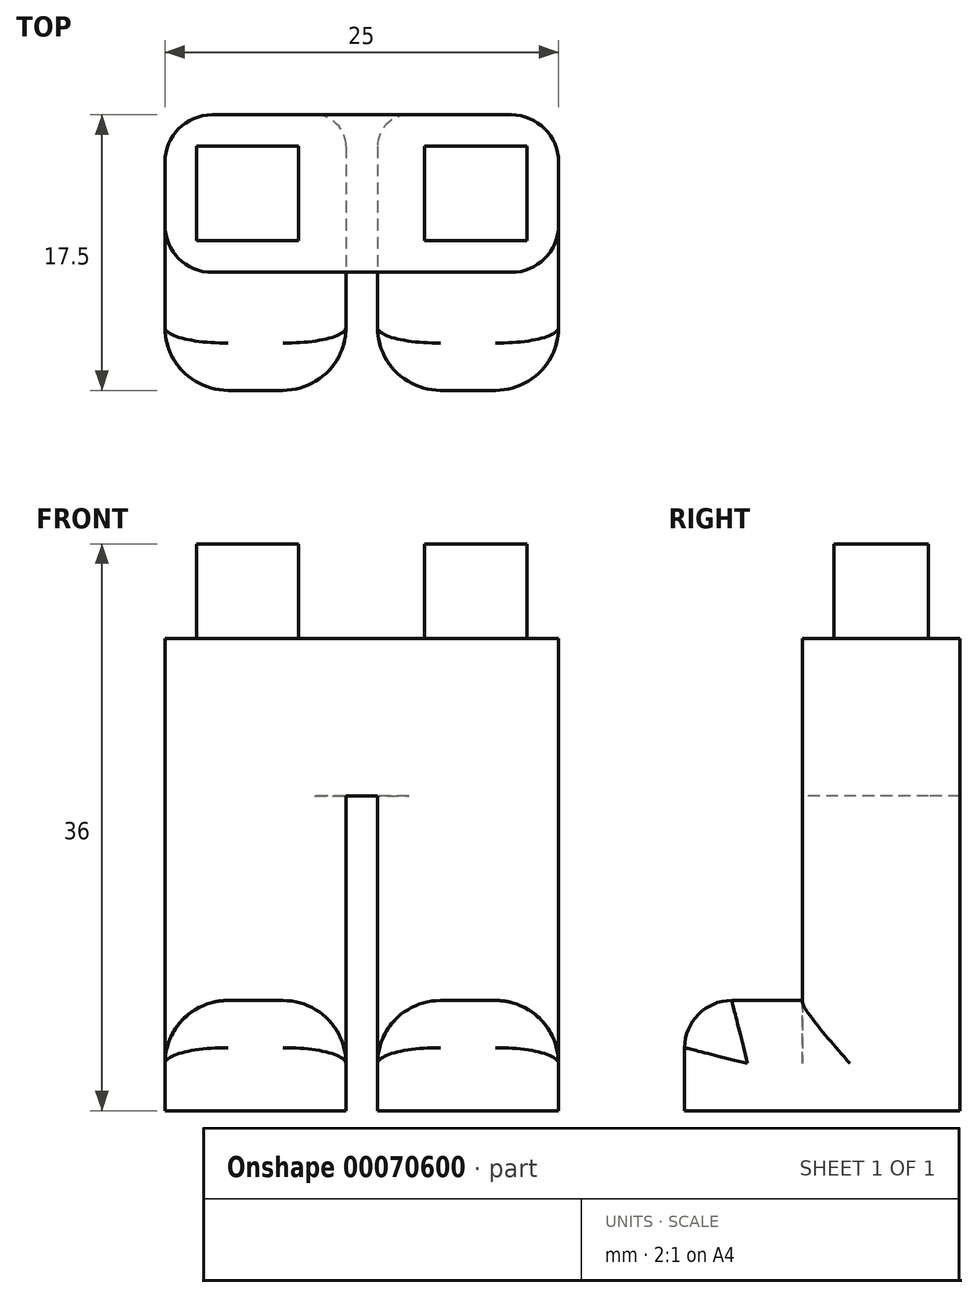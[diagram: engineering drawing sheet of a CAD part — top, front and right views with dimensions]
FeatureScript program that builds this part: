
annotation { "Feature Type Name" : "Feature", "Feature Type Description" : "" }
export const myFeature = defineFeature(function(context is Context, id is Id, definition is map)
    precondition{}
    {
        {
            var Q0;
            Q0=qCreatedBy(makeId("Top.planeOp"),FACE);
            var sketch = newSketch(context, id + "F0", { "sketchPlane" : qUnion([Q0])});
            skLineSegment(sketch, "E0.rect.bottom", {"start": v(-12.5, 5) * mm, "end": v(12.5, 5) * mm});
            skLineSegment(sketch, "E0.rect.top", {"start": v(-12.5, -5) * mm, "end": v(12.5, -5) * mm});
            skLineSegment(sketch, "E0.rect.left", {"start": v(-12.5, 5) * mm, "end": v(-12.5, -5) * mm});
            skLineSegment(sketch, "E0.rect.right", {"start": v(12.5, 5) * mm, "end": v(12.5, -5) * mm});
            skPoint(sketch, "E0.rect.middle", {"position": v(0, 0) * mm});
            skSolve(sketch);
        }
        {
            var Q0;
            Q0=makeQuery(id+"F0.imprint","IMPRINT",FACE,{"disambiguationData":[TD([[makeQuery(id+"F0.imprint","IMPRINT",EDGE,{"derivedFrom":sQuery(id+"F0.wireOp",EDGE,"E0.rect.bottom")}),-1.0]])]});
            extrude(context, id + "F1", {"entities" : qUnion([Q0]), "depth" : 30 * mm});
        }
        {
            var Q0;
            Q0=makeQuery(id+"F1.opExtrude","CAP_FACE",FACE,{"disambiguationData":[OSD([sQuery(id+"F0.wireOp",EDGE,"E0.rect.bottom"),sQuery(id+"F0.wireOp",EDGE,"E0.rect.top"),sQuery(id+"F0.wireOp",EDGE,"E0.rect.left"),sQuery(id+"F0.wireOp",EDGE,"E0.rect.right")])],"isStart":false});
            var sketch = newSketch(context, id + "F2", { "sketchPlane" : qUnion([Q0])});
            skLineSegment(sketch, "E1.bottom", {"start": v(-10.5, 3) * mm, "end": v(10.5, 3) * mm});
            skLineSegment(sketch, "E1.top", {"start": v(-10.5, -3) * mm, "end": v(10.5, -3) * mm});
            skLineSegment(sketch, "E1.left", {"start": v(-10.5, 3) * mm, "end": v(-10.5, -3) * mm});
            skLineSegment(sketch, "E1.right", {"start": v(10.5, 3) * mm, "end": v(10.5, -3) * mm});
            skLineSegment(sketch, "E2.bottom", {"start": v(-4, 3) * mm, "end": v(4, 3) * mm});
            skLineSegment(sketch, "E2.top", {"start": v(-4, -3) * mm, "end": v(4, -3) * mm});
            skLineSegment(sketch, "E2.left", {"start": v(-4, 3) * mm, "end": v(-4, -3) * mm});
            skLineSegment(sketch, "E2.right", {"start": v(4, 3) * mm, "end": v(4, -3) * mm});
            skSolve(sketch);
        }
        {
            var Q0;
            {var subQ0=sQuery(id+"F2.wireOp",EDGE,"E1.right");Q0=makeQuery(id+"F2.imprint","IMPRINT",FACE,{"disambiguationData":[TD([[makeQuery(id+"F2.imprint","IMPRINT",EDGE,{"derivedFrom":subQ0}),-1.0]])]});}
            var Q1;
            {var subQ0=sQuery(id+"F2.wireOp",EDGE,"E1.left");Q1=makeQuery(id+"F2.imprint","IMPRINT",FACE,{"disambiguationData":[TD([[makeQuery(id+"F2.imprint","IMPRINT",EDGE,{"derivedFrom":subQ0}),1.0]])]});}
            extrude(context, id + "F3", {"entities" : qUnion([Q0, Q1]), "operationType" : NewBodyOperationType.ADD, "depth" : 6 * mm});
        }
        {
            var Q0;
            Q0=makeQuery(id+"F1.opExtrude","SWEPT_FACE",FACE,{"disambiguationData":[OSD([sQuery(id+"F0.wireOp",EDGE,"E0.rect.top")])]});
            var sketch = newSketch(context, id + "F4", { "sketchPlane" : qUnion([Q0])});
            skLineSegment(sketch, "E3.bottom", {"start": v(1, 0) * mm, "end": v(-1, 0) * mm});
            skLineSegment(sketch, "E3.top", {"start": v(1, 20) * mm, "end": v(-1, 20) * mm});
            skLineSegment(sketch, "E3.left", {"start": v(1, 0) * mm, "end": v(1, 20) * mm});
            skLineSegment(sketch, "E3.right", {"start": v(-1, 0) * mm, "end": v(-1, 20) * mm});
            skLineSegment(sketch, "E4.bottom", {"start": v(-12.5, 0) * mm, "end": v(-1, 0) * mm});
            skLineSegment(sketch, "E4.top", {"start": v(-12.5, 7) * mm, "end": v(-1, 7) * mm});
            skLineSegment(sketch, "E4.left", {"start": v(-12.5, 0) * mm, "end": v(-12.5, 7) * mm});
            skLineSegment(sketch, "E4.right", {"start": v(-1, 0) * mm, "end": v(-1, 7) * mm});
            skLineSegment(sketch, "E5.bottom", {"start": v(12.5, 0) * mm, "end": v(1, 0) * mm});
            skLineSegment(sketch, "E5.top", {"start": v(12.5, 7) * mm, "end": v(1, 7) * mm});
            skLineSegment(sketch, "E5.left", {"start": v(12.5, 0) * mm, "end": v(12.5, 7) * mm});
            skLineSegment(sketch, "E5.right", {"start": v(1, 0) * mm, "end": v(1, 7) * mm});
            skSolve(sketch);
        }
        {
            var Q0;
            Q0=makeQuery(id+"F4.imprint","IMPRINT",FACE,{"disambiguationData":[TD([[makeQuery(id+"F4.imprint","IMPRINT",EDGE,{"derivedFrom":sQuery(id+"F4.wireOp",EDGE,"E3.bottom")}),1.0]])]});
            extrude(context, id + "F5", {"entities" : qUnion([Q0]), "operationType" : NewBodyOperationType.REMOVE, "endBound" : BoundingType.THROUGH_ALL, "oppositeDirection" : true, "depth" : 25 * mm});
        }
        {
            var Q0;
            Q0=makeQuery(id+"F4.imprint","IMPRINT",FACE,{"disambiguationData":[TD([[makeQuery(id+"F4.imprint","IMPRINT",EDGE,{"derivedFrom":sQuery(id+"F4.wireOp",EDGE,"E5.bottom")}),1.0]])]});
            var Q1;
            Q1=makeQuery(id+"F4.imprint","IMPRINT",FACE,{"disambiguationData":[TD([[makeQuery(id+"F4.imprint","IMPRINT",EDGE,{"derivedFrom":sQuery(id+"F4.wireOp",EDGE,"E4.bottom")}),1.0]])]});
            extrude(context, id + "F6", {"entities" : qUnion([Q0, Q1]), "operationType" : NewBodyOperationType.ADD, "depth" : 7.5 * mm});
        }
        {
            var Q0;
            Q0=makeQuery(id+"F6.opExtrude","CAP_EDGE",EDGE,{"disambiguationData":[OSD([sQuery(id+"F4.wireOp",EDGE,"E4.top")])],"isStart":false});
            var Q1;
            Q1=makeQuery(id+"F6.opExtrude","CAP_EDGE",EDGE,{"disambiguationData":[OSD([sQuery(id+"F4.wireOp",EDGE,"E5.top")])],"isStart":false});
            fillet(context, id + "F7", {"entities" : qUnion([Q0, Q1]), "radius" : 3 * mm, "tangentPropagation" : true, "allowEdgeOverflow" : false});
        }
        {
            var Q0;
            Q0=makeQuery(id+"F6.opExtrude","SWEPT_EDGE",EDGE,{"disambiguationData":[OSD([sQuery(id+"F0.wireOp",EDGE,"E0.rect.top"),sQuery(id+"F0.wireOp",EDGE,"E0.rect.right"),sQuery(id+"F4.wireOp",EDGE,"E5.top"),sQuery(id+"F4.wireOp",EDGE,"E5.left")])]});
            var Q1;
            Q1=makeQuery(id+"F6.opExtrude","SWEPT_EDGE",EDGE,{"disambiguationData":[OSD([sQuery(id+"F4.wireOp",EDGE,"E3.left"),sQuery(id+"F4.wireOp",EDGE,"E5.top"),sQuery(id+"F4.wireOp",EDGE,"E5.right")])]});
            var Q2;
            Q2=makeQuery(id+"F6.opExtrude","SWEPT_EDGE",EDGE,{"disambiguationData":[OSD([sQuery(id+"F4.wireOp",EDGE,"E3.right"),sQuery(id+"F4.wireOp",EDGE,"E4.top"),sQuery(id+"F4.wireOp",EDGE,"E4.right")])]});
            var Q3;
            Q3=makeQuery(id+"F6.opExtrude","SWEPT_EDGE",EDGE,{"disambiguationData":[OSD([sQuery(id+"F0.wireOp",EDGE,"E0.rect.top"),sQuery(id+"F0.wireOp",EDGE,"E0.rect.left"),sQuery(id+"F4.wireOp",EDGE,"E4.top"),sQuery(id+"F4.wireOp",EDGE,"E4.left")])]});
            fillet(context, id + "F8", {"entities" : qUnion([Q0, Q1, Q2, Q3]), "radius" : 4 * mm, "tangentPropagation" : true, "allowEdgeOverflow" : false});
        }
        {
            var Q0;
            Q0=makeQuery(id+"F1.opExtrude","SWEPT_EDGE",EDGE,{"disambiguationData":[OSD([sQuery(id+"F0.wireOp",EDGE,"E0.rect.top"),sQuery(id+"F0.wireOp",EDGE,"E0.rect.right")])]});
            var Q1;
            Q1=makeQuery(id+"F1.opExtrude","SWEPT_EDGE",EDGE,{"disambiguationData":[OSD([sQuery(id+"F0.wireOp",EDGE,"E0.rect.bottom"),sQuery(id+"F0.wireOp",EDGE,"E0.rect.right")])]});
            var Q2;
            Q2=makeQuery(id+"F1.opExtrude","SWEPT_EDGE",EDGE,{"disambiguationData":[OSD([sQuery(id+"F0.wireOp",EDGE,"E0.rect.top"),sQuery(id+"F0.wireOp",EDGE,"E0.rect.left")])]});
            var Q3;
            Q3=makeQuery(id+"F1.opExtrude","SWEPT_EDGE",EDGE,{"disambiguationData":[OSD([sQuery(id+"F0.wireOp",EDGE,"E0.rect.bottom"),sQuery(id+"F0.wireOp",EDGE,"E0.rect.left")])]});
            fillet(context, id + "F9", {"entities" : qUnion([Q0, Q1, Q2, Q3]), "radius" : 3 * mm, "tangentPropagation" : true, "allowEdgeOverflow" : false});
        }
        {
            var Q0;
            Q0=makeQuery(id+"F5.boolean.opBoolean","COPY",EDGE,{"derivedFrom":makeQuery(id+"F5.opExtrude","CAP_EDGE",EDGE,{"disambiguationData":[OSD([sQuery(id+"F4.wireOp",EDGE,"E3.right"),sQuery(id+"F4.wireOp",EDGE,"E4.right")])],"isStart":true})});
            var Q1;
            Q1=makeQuery(id+"F5.boolean.opBoolean","COPY",EDGE,{"derivedFrom":makeQuery(id+"F5.opExtrude","CAP_EDGE",EDGE,{"disambiguationData":[OSD([sQuery(id+"F4.wireOp",EDGE,"E3.left"),sQuery(id+"F4.wireOp",EDGE,"E5.right")])],"isStart":true})});
            var Q2;
            Q2=makeQuery(id+"F5.boolean.opBoolean","INTERSECT",EDGE,{"derivedFrom":[makeQuery(id+"F1.opExtrude","SWEPT_FACE",FACE,{"disambiguationData":[OSD([sQuery(id+"F0.wireOp",EDGE,"E0.rect.bottom")])]}),makeQuery(id+"F5.opExtrude","SWEPT_FACE",FACE,{"disambiguationData":[OSD([sQuery(id+"F4.wireOp",EDGE,"E3.right"),sQuery(id+"F4.wireOp",EDGE,"E4.right")])]})]});
            var Q3;
            Q3=makeQuery(id+"F5.boolean.opBoolean","INTERSECT",EDGE,{"derivedFrom":[makeQuery(id+"F1.opExtrude","SWEPT_FACE",FACE,{"disambiguationData":[OSD([sQuery(id+"F0.wireOp",EDGE,"E0.rect.bottom")])]}),makeQuery(id+"F5.opExtrude","SWEPT_FACE",FACE,{"disambiguationData":[OSD([sQuery(id+"F4.wireOp",EDGE,"E3.left"),sQuery(id+"F4.wireOp",EDGE,"E5.right")])]})]});
            fillet(context, id + "F10", {"entities" : qUnion([Q0, Q1, Q2, Q3]), "radius" : 2 * mm, "tangentPropagation" : true, "allowEdgeOverflow" : false});
        }
    });
